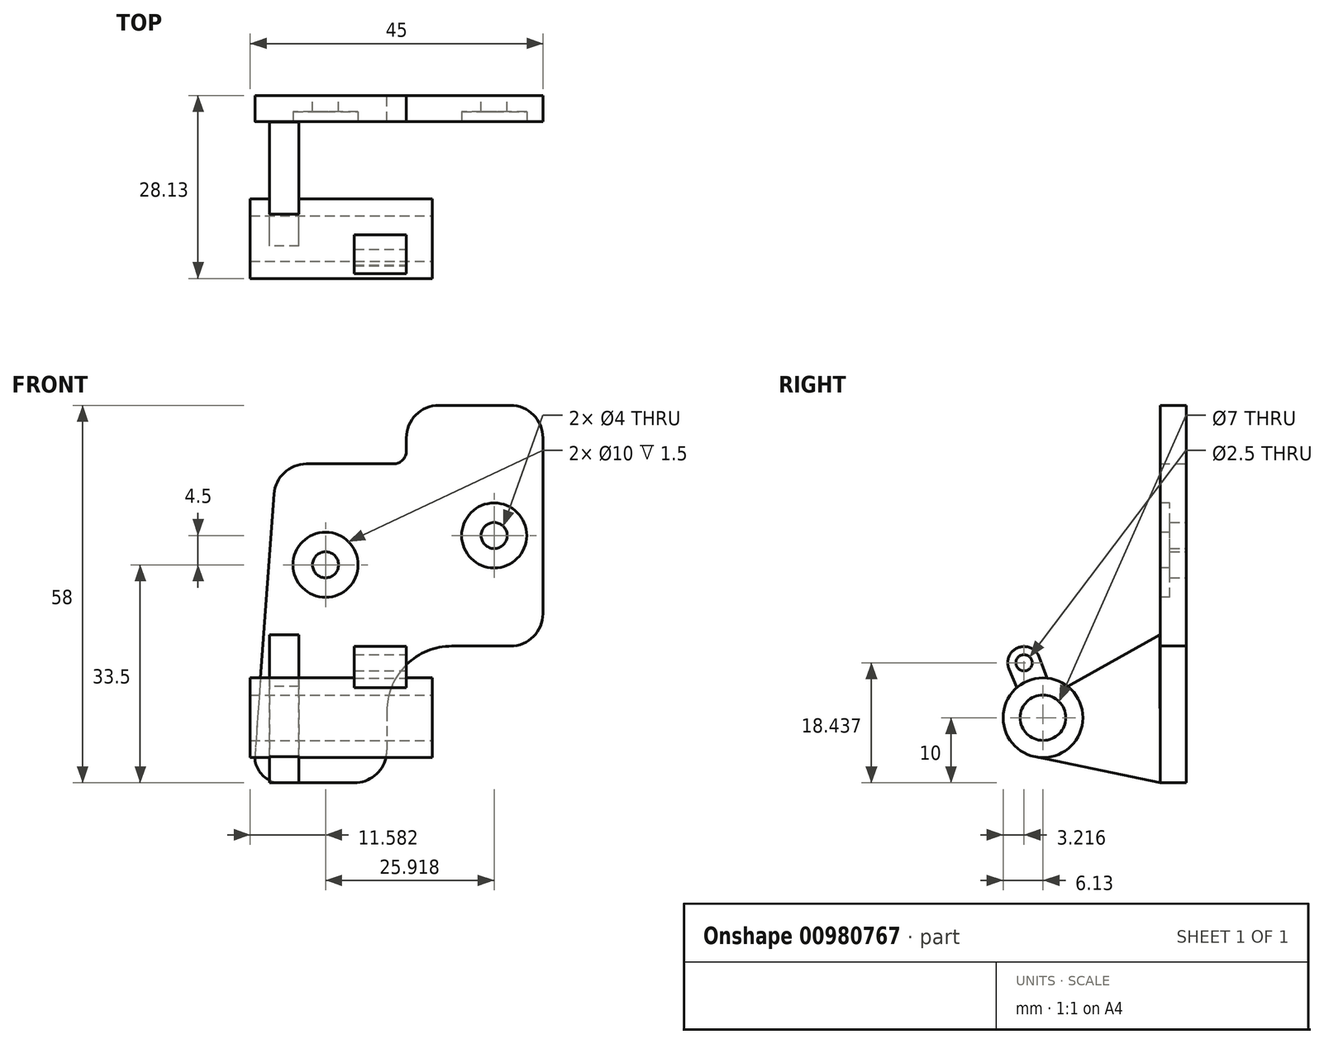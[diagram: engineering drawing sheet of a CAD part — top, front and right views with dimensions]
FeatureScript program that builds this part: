
annotation { "Feature Type Name" : "Feature", "Feature Type Description" : "" }
export const myFeature = defineFeature(function(context is Context, id is Id, definition is map)
    precondition{}
    {
        {
            var Q0;
            Q0=qCreatedBy(makeId("Front.planeOp"),FACE);
            var sketch = newSketch(context, id + "F0", { "sketchPlane" : qUnion([Q0]), "disableImprinting" : false});
            skLineSegment(sketch, "E0.bottom", {"start": v(7, 0) * mm, "end": v(16, 0) * mm});
            skLineSegment(sketch, "E0.top", {"start": v(5, 37) * mm, "end": v(16, 37) * mm});
            skLineSegment(sketch, "E0.left", {"start": v(0, 30) * mm, "end": v(0, 32) * mm});
            skLineSegment(sketch, "E0.right", {"start": v(21, 5) * mm, "end": v(21, 32) * mm});
            skLineSegment(sketch, "E1.top", {"start": v(-19.29, -21) * mm, "end": v(-8, -21) * mm});
            skLineSegment(sketch, "E1.left", {"start": v(-20.34, 23.37) * mm, "end": v(-23.28, -16.7) * mm});
            skLineSegment(sketch, "E1.right", {"start": v(-3, -10) * mm, "end": v(-3, -16) * mm});
            skPoint(sketch, "E2.visualSharp", {"position": v(21, 37) * mm});
            skArc(sketch, "E2.filletArc", {"start": v(21, 32) * mm, "mid": v(19.54, 35.54) * mm, "end": v(16, 37) * mm});
            skPoint(sketch, "E3.visualSharp", {"position": v(0, 37) * mm});
            skArc(sketch, "E3.filletArc", {"start": v(5, 37) * mm, "mid": v(1.46, 35.54) * mm, "end": v(0, 32) * mm});
            skPoint(sketch, "E4.visualSharp", {"position": v(21, 0) * mm});
            skArc(sketch, "E4.filletArc", {"start": v(16, 0) * mm, "mid": v(19.54, 1.46) * mm, "end": v(21, 5) * mm});
            skPoint(sketch, "E5.visualSharp", {"position": v(-3, -21) * mm});
            skArc(sketch, "E5.filletArc", {"start": v(-8, -21) * mm, "mid": v(-4.46, -19.54) * mm, "end": v(-3, -16) * mm});
            skPoint(sketch, "E6.orphan", {"position": v(0, 0) * mm});
            skPoint(sketch, "E7.visualSharp", {"position": v(-3, 0) * mm});
            skArc(sketch, "E7.filletArc", {"start": v(7, 0) * mm, "mid": v(-0.07, -2.93) * mm, "end": v(-3, -10) * mm});
            skPoint(sketch, "E8.visualSharp", {"position": v(0, 28) * mm});
            skCircle(sketch, "E9", {"center": v(13.5, 17) * mm, "radius": 2 * mm});
            skLineSegment(sketch, "E10", {"start": v(-15.35, 28) * mm, "end": v(-2, 28) * mm});
            skCircle(sketch, "E11", {"center": v(-12.42, 12.5) * mm, "radius": 2 * mm});
            skPoint(sketch, "E12.visualSharp", {"position": v(-20, 28) * mm});
            skArc(sketch, "E12.filletArc", {"start": v(-15.35, 28) * mm, "mid": v(-18.76, 26.66) * mm, "end": v(-20.34, 23.37) * mm});
            skArc(sketch, "E13.filletArc", {"start": v(-2, 28) * mm, "mid": v(-0.59, 28.59) * mm, "end": v(0, 30) * mm});
            skPoint(sketch, "E14.visualSharp", {"position": v(-23.6, -21) * mm});
            skArc(sketch, "E14.filletArc", {"start": v(-23.28, -16.7) * mm, "mid": v(-22.22, -19.72) * mm, "end": v(-19.29, -21) * mm});
            skSolve(sketch);
        }
        {
            var Q0;
            Q0=makeQuery(id+"F0.imprint","IMPRINT",FACE,{"disambiguationData":[TD([[makeQuery(id+"F0.imprint","IMPRINT",EDGE,{"derivedFrom":sQuery(id+"F0.wireOp",EDGE,"E0.bottom")}),1.0]])]});
            extrude(context, id + "F1", {"entities" : qUnion([Q0]), "depth" : 4 * mm, "offsetDistance" : 25 * mm});
        }
        {
            var Q0;
            Q0=makeQuery(id+"F1.opExtrude","CAP_FACE",FACE,{"disambiguationData":[OSD([sQuery(id+"F0.wireOp",EDGE,"E0.bottom"),sQuery(id+"F0.wireOp",EDGE,"E0.top"),sQuery(id+"F0.wireOp",EDGE,"E0.left"),sQuery(id+"F0.wireOp",EDGE,"E0.right"),sQuery(id+"F0.wireOp",EDGE,"E1.top"),sQuery(id+"F0.wireOp",EDGE,"E1.left"),sQuery(id+"F0.wireOp",EDGE,"E1.right"),sQuery(id+"F0.wireOp",EDGE,"E2.filletArc"),sQuery(id+"F0.wireOp",EDGE,"E3.filletArc"),sQuery(id+"F0.wireOp",EDGE,"E4.filletArc"),sQuery(id+"F0.wireOp",EDGE,"E5.filletArc"),sQuery(id+"F0.wireOp",EDGE,"E7.filletArc"),sQuery(id+"F0.wireOp",EDGE,"E9"),sQuery(id+"F0.wireOp",EDGE,"E10"),sQuery(id+"F0.wireOp",EDGE,"E11"),sQuery(id+"F0.wireOp",EDGE,"E12.filletArc"),sQuery(id+"F0.wireOp",EDGE,"E13.filletArc")])],"isStart":false});
            var sketch = newSketch(context, id + "F2", { "sketchPlane" : qUnion([Q0])});
            skCircle(sketch, "E15", {"center": v(-12.42, 12.5) * mm, "radius": 5 * mm});
            skCircle(sketch, "E16", {"center": v(13.5, 17) * mm, "radius": 5 * mm});
            skSolve(sketch);
        }
        {
            var Q0;
            Q0 = qSketchRegion(id + "F2", true);
            extrude(context, id + "F3", {"entities" : qUnion([Q0]), "operationType" : NewBodyOperationType.REMOVE, "oppositeDirection" : true, "depth" : 1.5 * mm, "offsetDistance" : 25 * mm});
        }
        {
            var Q0;
            Q0=qCreatedBy(makeId("Right.planeOp"),FACE);
            var sketch = newSketch(context, id + "F4", { "sketchPlane" : qUnion([Q0])});
            skCircle(sketch, "E17", {"center": v(-22, -11) * mm, "radius": 6.12 * mm});
            skCircle(sketch, "E18", {"center": v(-22, -11) * mm, "radius": 3.5 * mm});
            skSolve(sketch);
        }
        {
            var Q0;
            Q0=makeQuery(id+"F4.imprint","IMPRINT",FACE,{"disambiguationData":[TD([[makeQuery(id+"F4.imprint","IMPRINT",EDGE,{"derivedFrom":sQuery(id+"F4.wireOp",EDGE,"E17")}),1.0]])]});
            extrude(context, id + "F5", {"entities" : qUnion([Q0]), "oppositeDirection" : true, "depth" : 20 * mm, "offsetDistance" : 25 * mm});
        }
        {
            var Q0;
            Q0=makeQuery(id+"F5.opExtrude","CAP_FACE",FACE,{"disambiguationData":[OSD([sQuery(id+"F4.wireOp",EDGE,"E17"),sQuery(id+"F4.wireOp",EDGE,"E18")])],"isStart":true});
            var sketch = newSketch(context, id + "F6", { "sketchPlane" : qUnion([Q0])});
            skCircle(sketch, "E19", {"center": v(-24.91, -2.56) * mm, "radius": 2.5 * mm});
            skCircle(sketch, "E20", {"center": v(-24.91, -2.56) * mm, "radius": 1.25 * mm});
            skLineSegment(sketch, "E21", {"start": v(-22.57, -1.7) * mm, "end": v(-21.4, -4.9) * mm});
            skLineSegment(sketch, "E22", {"start": v(-27.22, -3.52) * mm, "end": v(-26.04, -6.4) * mm});
            skSolve(sketch);
        }
        {
            var Q0;
            Q0=makeQuery(id+"F6.imprint","IMPRINT",FACE,{"disambiguationData":[TD([[makeQuery(id+"F6.imprint","IMPRINT",EDGE,{"derivedFrom":sQuery(id+"F6.wireOp",EDGE,"E20")}),-1.0]])]});
            var Q1;
            {var subQ0=sQuery(id+"F6.wireOp",EDGE,"E21");Q1=makeQuery(id+"F6.imprint","IMPRINT",FACE,{"disambiguationData":[TD([[makeQuery(id+"F6.imprint","IMPRINT",EDGE,{"derivedFrom":subQ0}),-1.0]])]});}
            extrude(context, id + "F7", {"entities" : qUnion([Q0, Q1]), "oppositeDirection" : true, "depth" : 8 * mm, "offsetDistance" : 8 * mm});
        }
        {
            var Q0;
            Q0 = qSketchRegion(id + "F4", true);
            extrude(context, id + "F8", {"entities" : qUnion([Q0]), "operationType" : NewBodyOperationType.ADD, "depth" : 4 * mm, "offsetDistance" : 25 * mm});
        }
        {
            var Q0;
            Q0=makeQuery(id+"F5.opExtrude","CAP_FACE",FACE,{"disambiguationData":[OSD([sQuery(id+"F4.wireOp",EDGE,"E17"),sQuery(id+"F4.wireOp",EDGE,"E18")])],"isStart":false});
            var sketch = newSketch(context, id + "F9", { "sketchPlane" : qUnion([Q0])});
            skLineSegment(sketch, "E23", {"start": v(23.36, -16.97) * mm, "end": v(4, -21) * mm});
            skLineSegment(sketch, "E24", {"start": v(18.23, -6.17) * mm, "end": v(4.06, 1.74) * mm});
            skLineSegment(sketch, "E25", {"start": v(4.06, 1.74) * mm, "end": v(4, -21) * mm});
            skSolve(sketch);
        }
        {
            var Q0;
            Q0 = qSketchRegion(id + "F9", true);
            var Q1;
            {var subQ4=sQuery(id+"F9.wireOp",EDGE,"E24");Q1=makeQuery(id+"F9.imprint","IMPRINT",FACE,{"disambiguationData":[TD([[makeQuery(id+"F9.imprint","IMPRINT",EDGE,{"derivedFrom":subQ4}),1.0]])]});}
            extrude(context, id + "F10", {"entities" : qUnion([Q0, Q1]), "operationType" : NewBodyOperationType.ADD, "oppositeDirection" : true, "depth" : 3.5 * mm, "offsetDistance" : 25 * mm, "hasSecondDirection" : true, "secondDirectionOppositeDirection" : false, "secondDirectionDepth" : 1 * mm});
        }
        {
            var Q0;
            Q0=makeQuery(id+"F5.opExtrude","CAP_FACE",FACE,{"disambiguationData":[OSD([sQuery(id+"F4.wireOp",EDGE,"E17"),sQuery(id+"F4.wireOp",EDGE,"E18")])],"isStart":false});
            extrude(context, id + "F11", {"entities" : qUnion([Q0]), "operationType" : NewBodyOperationType.ADD, "depth" : 4 * mm, "offsetDistance" : 25 * mm});
        }
        {
            var Q0;
            Q0=makeQuery(id+"F5.opExtrude","SWEPT_BODY",BODY,{"disambiguationData":[OSD([sQuery(id+"F4.wireOp",EDGE,"E17"),sQuery(id+"F4.wireOp",EDGE,"E18")])]});
            var Q1;
            Q1=makeQuery(id+"F7.opExtrude","SWEPT_BODY",BODY,{"disambiguationData":[OSD([sQuery(id+"F4.wireOp",EDGE,"E17"),sQuery(id+"F6.wireOp",EDGE,"E19"),sQuery(id+"F6.wireOp",EDGE,"E20"),sQuery(id+"F6.wireOp",EDGE,"E21"),sQuery(id+"F6.wireOp",EDGE,"E22")])]});
            var Q2;
            Q2=makeQuery(id+"F10.opExtrude","SWEPT_BODY",BODY,{"disambiguationData":[OSD([sQuery(id+"F4.wireOp",EDGE,"E17"),sQuery(id+"F9.wireOp",EDGE,"E23"),sQuery(id+"F9.wireOp",EDGE,"E24"),sQuery(id+"F9.wireOp",EDGE,"E25")])]});
            transform(context, id + "F12", {"entities" : qUnion([Q0, Q1, Q2]), "transformType" : TransformType.TRANSLATION_3D, "dx" : 0 * mm, "dy" : 0 * mm, "dz" : 0 * mm, "makeCopy" : false});
        }
    });
